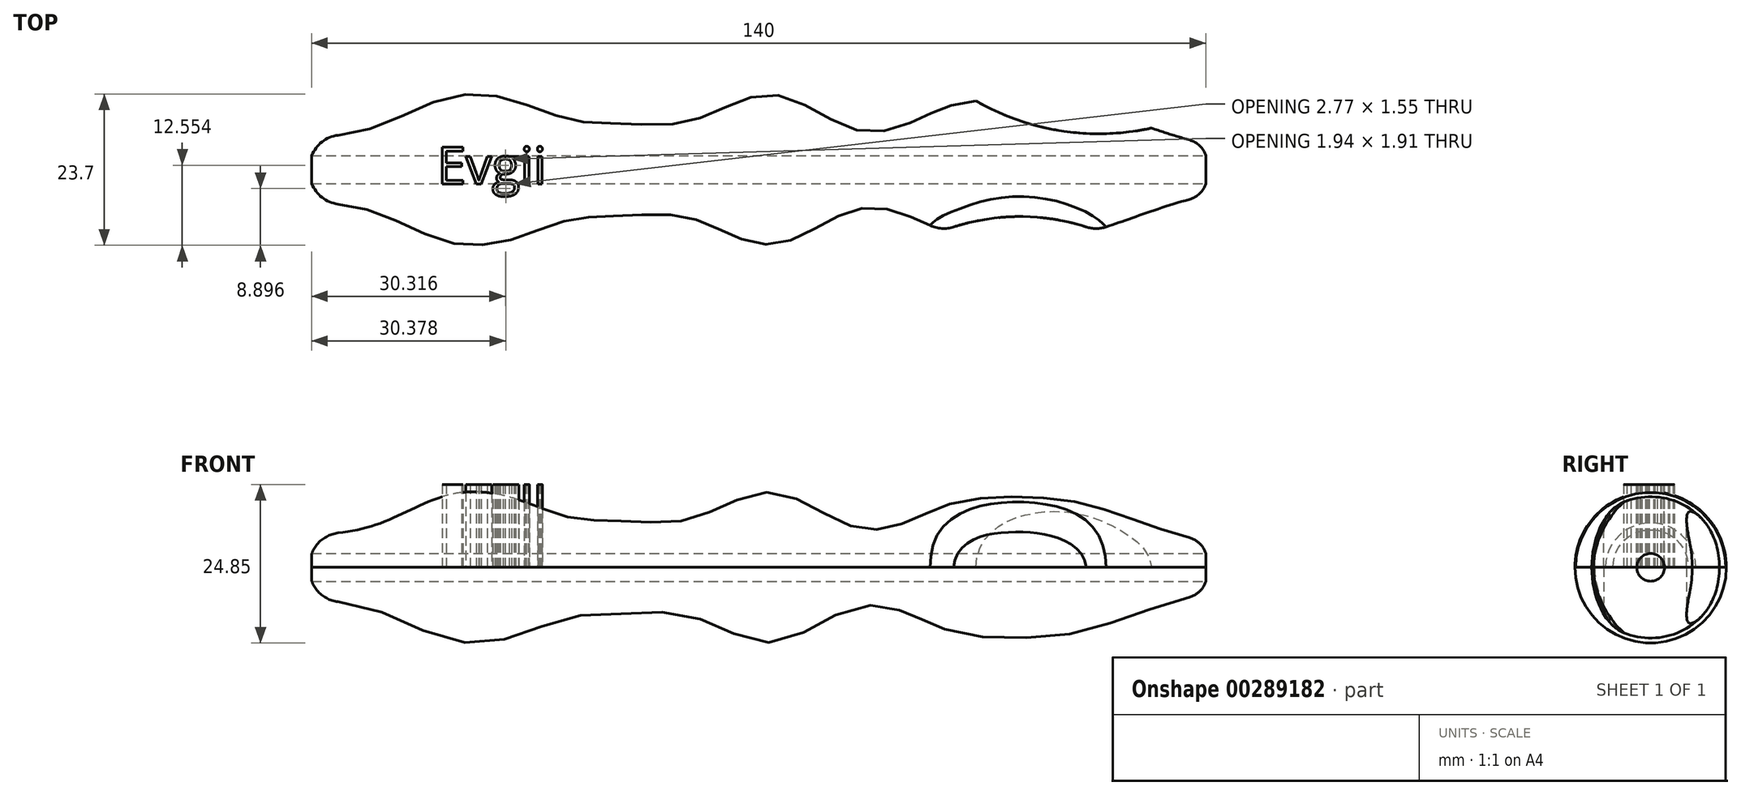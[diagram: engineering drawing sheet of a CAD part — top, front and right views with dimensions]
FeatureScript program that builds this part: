
annotation { "Feature Type Name" : "Feature", "Feature Type Description" : "" }
export const myFeature = defineFeature(function(context is Context, id is Id, definition is map)
    precondition{}
    {
        {
            var Q0;
            Q0=qCreatedBy(makeId("Top.planeOp"),FACE);
            var sketch = newSketch(context, id + "F0", { "sketchPlane" : qUnion([Q0])});
            skLineSegment(sketch, "E0", {"start": v(0, 0) * mm, "end": v(0, 5) * mm});
            skLineSegment(sketch, "E1", {"start": v(0, 0) * mm, "end": v(140, 0) * mm});
            skLineSegment(sketch, "E2", {"start": v(140, 0) * mm, "end": v(140, 4) * mm});
            skFitSpline(sketch, "E3", {"points": [v(0, 5) * mm, v(10.09, 6.7) * mm, v(21.34, 11.35) * mm, v(31.23, 10.96) * mm, v(40.34, 7.86) * mm, v(47.9, 7.27) * mm, v(57.8, 7.27) * mm, v(64.78, 9.8) * mm, v(72.15, 11.73) * mm, v(79.91, 8.63) * mm, v(87.28, 5.92) * mm, v(94.51, 7.68) * mm, v(98.98, 9.67) * mm, v(105.22, 10.9) * mm, v(116.7, 10.73) * mm, v(124.73, 8.86) * mm, v(140, 4) * mm], "startDerivative": vector(148.16, 12.96) * mm, "endDerivative": vector(196.67, -45.52) * mm});
            skSolve(sketch);
        }
        {
            var Q0;
            Q0=makeQuery(id+"F0.imprint","IMPRINT",FACE,{"disambiguationData":[TD([[makeQuery(id+"F0.imprint","IMPRINT",EDGE,{"derivedFrom":sQuery(id+"F0.wireOp",EDGE,"E0")}),-1.0]])]});
            var Q1;
            Q1=sQuery(id+"F0.wireOp",EDGE,"E1");
            revolve(context, id + "F1", {"entities" : qUnion([Q0]), "axis" : qUnion([Q1]), "revolveType" : RevolveType.ONE_DIRECTION, "angle" : 180 * degree});
        }
        {
            var Q0;
            Q0=qCreatedBy(makeId("Top.planeOp"),FACE);
            var sketch = newSketch(context, id + "F2", { "sketchPlane" : qUnion([Q0])});
            skCircle(sketch, "E4", {"center": v(110.9, -41.16) * mm, "radius": 33.8 * mm});
            skSolve(sketch);
        }
        {
            var Q0;
            Q0=makeQuery(id+"F1.opRevolve","SWEPT_FACE",FACE,{"disambiguationData":[OSD([sQuery(id+"F0.wireOp",EDGE,"E2")])]});
            var sketch = newSketch(context, id + "F3", { "sketchPlane" : qUnion([Q0])});
            skCircle(sketch, "E5", {"center": v(0, 0) * mm, "radius": 2.17 * mm});
            skSolve(sketch);
        }
        {
            var Q0;
            Q0=makeQuery(id+"F3.imprint","IMPRINT",FACE,{"disambiguationData":[TD([[makeQuery(id+"F3.imprint","IMPRINT",EDGE,{"derivedFrom":sQuery(id+"F3.wireOp",EDGE,"E5")}),1.0]])]});
            extrude(context, id + "F4", {"entities" : qUnion([Q0]), "operationType" : NewBodyOperationType.REMOVE, "endBound" : BoundingType.THROUGH_ALL, "oppositeDirection" : true, "depth" : 25.4 * mm});
        }
        {
            var Q0;
            Q0=makeQuery(id+"F1.opRevolve","SWEPT_EDGE",EDGE,{"disambiguationData":[OSD([sQuery(id+"F0.wireOp",EDGE,"E2"),sQuery(id+"F0.wireOp",EDGE,"E3")])]});
            fillet(context, id + "F5", {"entities" : qUnion([Q0]), "radius" : 3.66 * mm, "tangentPropagation" : true, "allowEdgeOverflow" : false});
        }
        {
            var Q0;
            Q0=makeQuery(id+"F1.opRevolve","SWEPT_EDGE",EDGE,{"disambiguationData":[OSD([sQuery(id+"F0.wireOp",EDGE,"E0"),sQuery(id+"F0.wireOp",EDGE,"E3")])]});
            fillet(context, id + "F6", {"entities" : qUnion([Q0]), "radius" : 5.08 * mm, "tangentPropagation" : true, "allowEdgeOverflow" : false});
        }
        {
            var Q0;
            Q0 = qSketchRegion(id + "F2", true);
            extrude(context, id + "F7", {"entities" : qUnion([Q0]), "operationType" : NewBodyOperationType.REMOVE, "endBound" : BoundingType.SYMMETRIC, "oppositeDirection" : true, "depth" : 25.4 * mm});
        }
        {
            var Q0;
            Q0=qCreatedBy(makeId("Top.planeOp"),FACE);
            var sketch = newSketch(context, id + "F8", { "sketchPlane" : qUnion([Q0])});
            skCircle(sketch, "E6", {"center": v(123.23, 44.1) * mm, "radius": 38.48 * mm});
            skSolve(sketch);
        }
        {
            var Q0;
            Q0=makeQuery(id+"F8.imprint","IMPRINT",FACE,{"disambiguationData":[TD([[makeQuery(id+"F8.imprint","IMPRINT",EDGE,{"derivedFrom":sQuery(id+"F8.wireOp",EDGE,"E6")}),1.0]])]});
            extrude(context, id + "F9", {"entities" : qUnion([Q0]), "operationType" : NewBodyOperationType.REMOVE, "endBound" : BoundingType.SYMMETRIC, "oppositeDirection" : true, "depth" : 25.4 * mm});
        }
        {
            var Q0;
            Q0=makeQuery(id+"F7.boolean.opBoolean","INTERSECT",EDGE,{"derivedFrom":[makeQuery(id+"F1.opRevolve","SWEPT_FACE",FACE,{"disambiguationData":[OSD([sQuery(id+"F0.wireOp",EDGE,"E3")])]}),makeQuery(id+"F7.opExtrude","SWEPT_FACE",FACE,{"disambiguationData":[OSD([sQuery(id+"F2.wireOp",EDGE,"E4")])]})]});
            fillet(context, id + "F10", {"entities" : qUnion([Q0]), "radius" : 5.08 * mm, "tangentPropagation" : true, "allowEdgeOverflow" : false});
        }
        {
            var Q0;
            Q0=makeQuery(id+"F1.opRevolve","SWEPT_BODY",BODY,{"disambiguationData":[OSD([sQuery(id+"F0.wireOp",EDGE,"E0"),sQuery(id+"F0.wireOp",EDGE,"E1"),sQuery(id+"F0.wireOp",EDGE,"E2"),sQuery(id+"F0.wireOp",EDGE,"E3")])]});
            var Q1;
            Q1=qCreatedBy(makeId("Top.planeOp"),FACE);
            mirror(context, id + "F11", {"entities" : qUnion([Q0]), "mirrorPlane" : qUnion([Q1])});
        }
        {
            var Q0;
            Q0=qCreatedBy(makeId("Top.planeOp"),FACE);
            var sketch = newSketch(context, id + "F12", { "sketchPlane" : qUnion([Q0])});
            skText(sketch, "E7", { "text": "Evgii", "fontName": "OpenSans-Regular.ttf"});
            const initialGuessF12  = {"E7": [0.01963, -0.00228, 1, 0, 0.00584]};
            skSetInitialGuess(sketch, initialGuessF12);
            skSolve(sketch);
        }
        {
            var Q0;
            Q0 = qSketchRegion(id + "F12", true);
            extrude(context, id + "F13", {"entities" : qUnion([Q0]), "depth" : 13 * mm});
        }
    });
